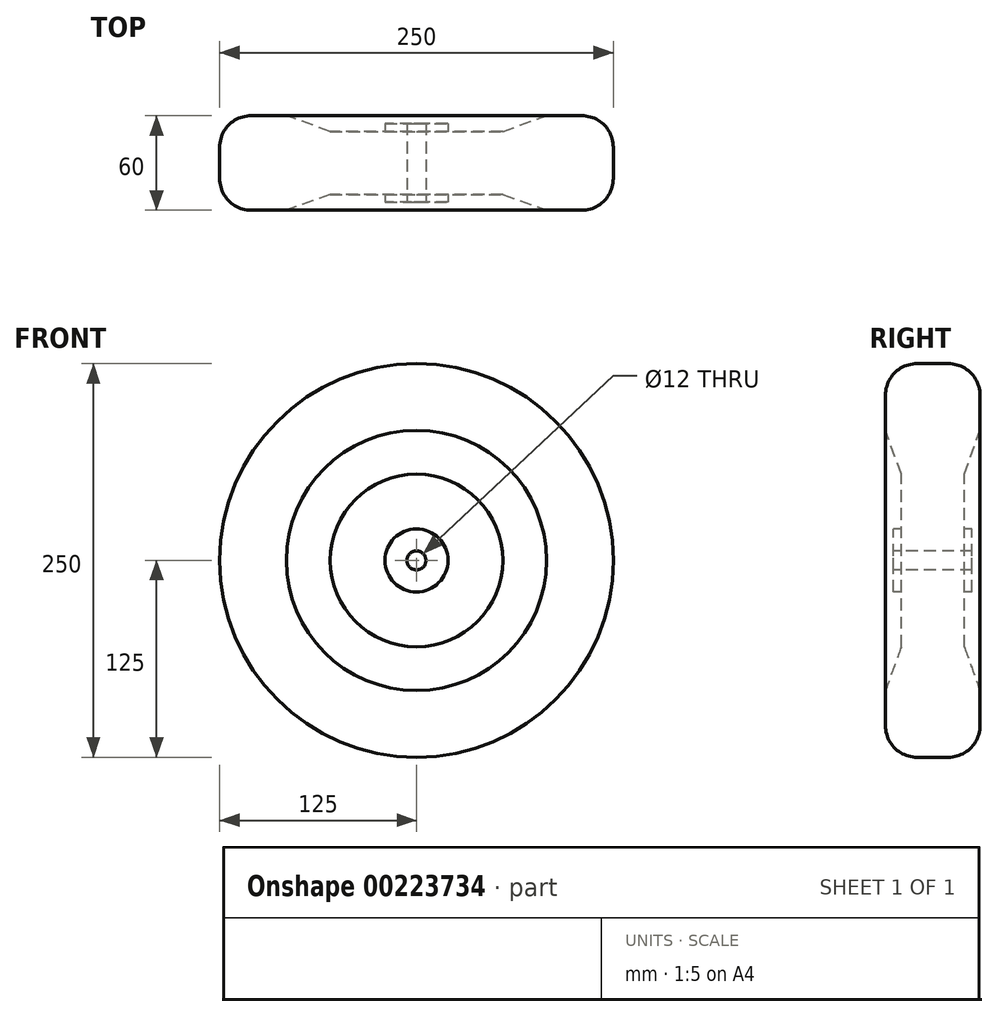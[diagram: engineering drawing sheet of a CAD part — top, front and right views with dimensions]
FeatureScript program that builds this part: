
annotation { "Feature Type Name" : "Feature", "Feature Type Description" : "" }
export const myFeature = defineFeature(function(context is Context, id is Id, definition is map)
    precondition{}
    {
        {
            var Q0;
            Q0=qCreatedBy(makeId("Right.planeOp"),FACE);
            var sketch = newSketch(context, id + "F0", { "sketchPlane" : qUnion([Q0])});
            skLineSegment(sketch, "E0", {"start": v(-26.49, 0) * mm, "end": v(27.33, 0) * mm, "construction": true});
            skLineSegment(sketch, "E1", {"start": v(-21.87, 6) * mm, "end": v(29.25, 6) * mm, "construction": true});
            skLineSegment(sketch, "E2", {"start": v(-20, 54.8) * mm, "end": v(-30, 82.62) * mm});
            skLineSegment(sketch, "E3", {"start": v(-30, 82.62) * mm, "end": v(-30, 125) * mm});
            skLineSegment(sketch, "E4", {"start": v(-30, 125) * mm, "end": v(0, 125) * mm});
            skLineSegment(sketch, "E5.MirrorCS", {"start": v(21.87, 6) * mm, "end": v(-29.25, 6) * mm, "construction": true});
            skLineSegment(sketch, "E6.MirrorCS", {"start": v(0, 6) * mm, "end": v(20, 6) * mm});
            skLineSegment(sketch, "E7.MirrorCS", {"start": v(20, 54.8) * mm, "end": v(30, 82.62) * mm});
            skLineSegment(sketch, "E8.MirrorCS", {"start": v(30, 82.62) * mm, "end": v(30, 125) * mm});
            skLineSegment(sketch, "E9.MirrorCS", {"start": v(30, 125) * mm, "end": v(0, 125) * mm});
            skLineSegment(sketch, "E10", {"start": v(-20, 54.8) * mm, "end": v(-20, 20) * mm});
            skLineSegment(sketch, "E11", {"start": v(-20, 20) * mm, "end": v(-25, 20) * mm});
            skLineSegment(sketch, "E12", {"start": v(-25, 20) * mm, "end": v(-25, 6) * mm});
            skLineSegment(sketch, "E13", {"start": v(-25, 6) * mm, "end": v(0, 6) * mm});
            skLineSegment(sketch, "E14.MirrorCS", {"start": v(20, 54.8) * mm, "end": v(20, 20) * mm});
            skLineSegment(sketch, "E15.MirrorCS", {"start": v(20, 20) * mm, "end": v(25, 20) * mm});
            skLineSegment(sketch, "E16.MirrorCS", {"start": v(25, 20) * mm, "end": v(25, 6) * mm});
            skLineSegment(sketch, "E17.MirrorCS", {"start": v(25, 6) * mm, "end": v(0, 6) * mm});
            skSolve(sketch);
        }
        {
            var Q0;
            Q0=qSketchRegion(id+"F0",true);
            var Q1;
            Q1=sQuery(id+"F0.wireOp",EDGE,"E0");
            revolve(context, id + "F1", {"entities" : qUnion([Q0]), "axis" : qUnion([Q1]), "revolveType" : RevolveType.FULL});
        }
        {
            var Q0;
            Q0=makeQuery(id+"F1.opRevolve","SWEPT_EDGE",EDGE,{"disambiguationData":[OSD([sQuery(id+"F0.wireOp",EDGE,"E3"),sQuery(id+"F0.wireOp",EDGE,"E4")])]});
            var Q1;
            Q1=makeQuery(id+"F1.opRevolve","SWEPT_EDGE",EDGE,{"disambiguationData":[OSD([sQuery(id+"F0.wireOp",EDGE,"E8.MirrorCS"),sQuery(id+"F0.wireOp",EDGE,"E9.MirrorCS")])]});
            fillet(context, id + "F2", {"entities" : qUnion([Q0, Q1]), "radius" : 20 * mm, "tangentPropagation" : true, "allowEdgeOverflow" : false});
        }
    });
